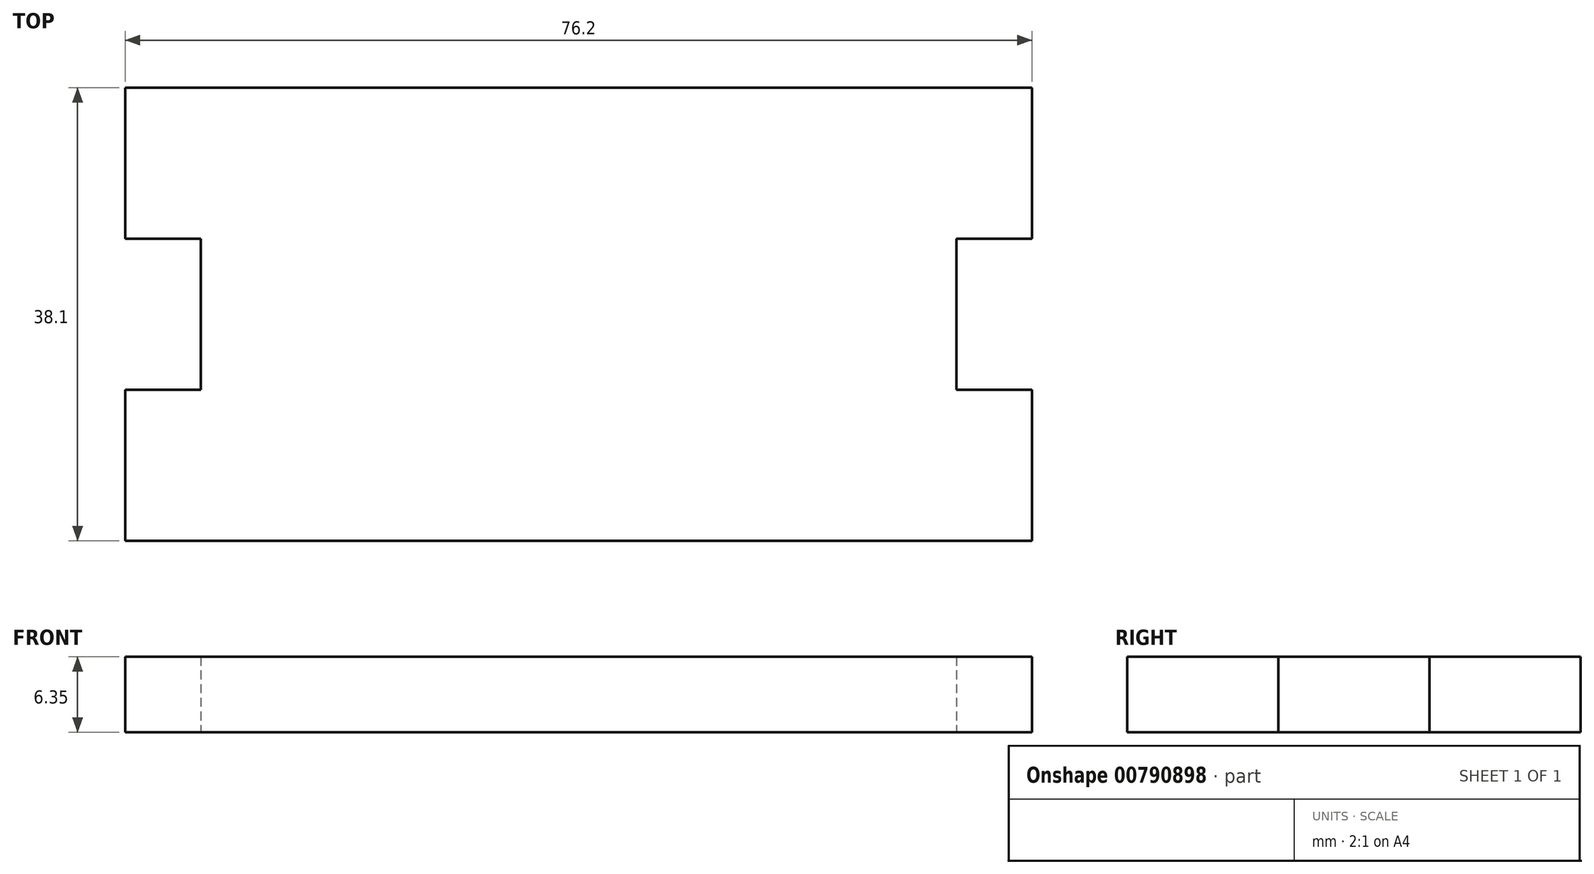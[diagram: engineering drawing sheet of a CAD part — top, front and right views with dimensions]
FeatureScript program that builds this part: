
annotation { "Feature Type Name" : "Feature", "Feature Type Description" : "" }
export const myFeature = defineFeature(function(context is Context, id is Id, definition is map)
    precondition{}
    {
        {
            var Q0;
            Q0=qCreatedBy(makeId("Top.planeOp"),FACE);
            var sketch = newSketch(context, id + "F0", { "sketchPlane" : qUnion([Q0])});
            skLineSegment(sketch, "E0.top", {"start": v(12.7, -55.09) * mm, "end": v(-63.5, -55.09) * mm});
            skLineSegment(sketch, "E0.left", {"start": v(12.7, -16.99) * mm, "end": v(12.7, -55.09) * mm});
            skLineSegment(sketch, "E0.right", {"start": v(-63.5, -16.99) * mm, "end": v(-63.5, -55.09) * mm});
            skLineSegment(sketch, "E1.0.3.0", {"start": v(-57.15, -29.69) * mm, "end": v(-57.15, -42.39) * mm});
            skLineSegment(sketch, "E1.0.3.1", {"start": v(-63.5, -29.69) * mm, "end": v(-63.5, -42.39) * mm});
            skLineSegment(sketch, "E1.0.3.2", {"start": v(-63.5, -29.69) * mm, "end": v(-57.15, -29.69) * mm});
            skLineSegment(sketch, "E1.0.3.3", {"start": v(-63.5, -42.39) * mm, "end": v(-57.15, -42.39) * mm});
            skLineSegment(sketch, "E1.1.3.0", {"start": v(12.7, -29.69) * mm, "end": v(12.7, -42.39) * mm});
            skLineSegment(sketch, "E1.1.3.1", {"start": v(6.35, -29.69) * mm, "end": v(6.35, -42.39) * mm});
            skLineSegment(sketch, "E1.1.3.2", {"start": v(6.35, -29.69) * mm, "end": v(12.7, -29.69) * mm});
            skLineSegment(sketch, "E1.1.3.3", {"start": v(6.35, -42.39) * mm, "end": v(12.7, -42.39) * mm});
            skLineSegment(sketch, "E2", {"start": v(-63.5, -16.99) * mm, "end": v(12.7, -16.99) * mm});
            skSolve(sketch);
        }
        {
            var Q0;
            {var subQ20=sQuery(id+"F0.wireOp",EDGE,"E0.top");Q0=makeQuery(id+"F0.imprint","IMPRINT",FACE,{"disambiguationData":[TD([[makeQuery(id+"F0.imprint","IMPRINT",EDGE,{"derivedFrom":subQ20}),-1.0]])]});}
            extrude(context, id + "F1", {"entities" : qUnion([Q0]), "depth" : 6.35 * mm, "offsetDistance" : 25.4 * mm});
        }
    });
